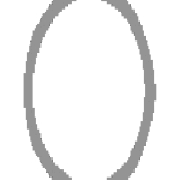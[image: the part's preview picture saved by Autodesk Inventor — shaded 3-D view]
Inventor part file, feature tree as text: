
AUTODESK INVENTOR PART (.ipt)
format: ipt  version: 2021 (Build 250183000, 183)  size: 109,568 bytes
history: native  units: in
note: dims shown in document units (in); Inventor stores cm internally (conversion verified against a paired STEP export)
features: other x4, sketch x3, plane x1
ambient origin geometry x8: Origin, YZ Plane, XZ Plane, XY Plane, X Axis, Y Axis, Z Axis, Center Point
bodies: Solid1 (feature_tree), Body (feature_tree)
feature tree (8):
  other  "Driven Length"
  other  "Frame Generator"
  other  "Start Plane"
  other  "End Plane"
  sketch  "Sketch"  dims[d2=22.3842in d4=-0.0in d5=22.3842in d6=0.12in d7=0.0in d8=90.0deg d9=22.3842in]
  sketch  "Sketch2"  dims[d0=1.0in]
  plane  "Work Plane3"
  sketch  "Sketch3"  dims[d1=0.065in]
